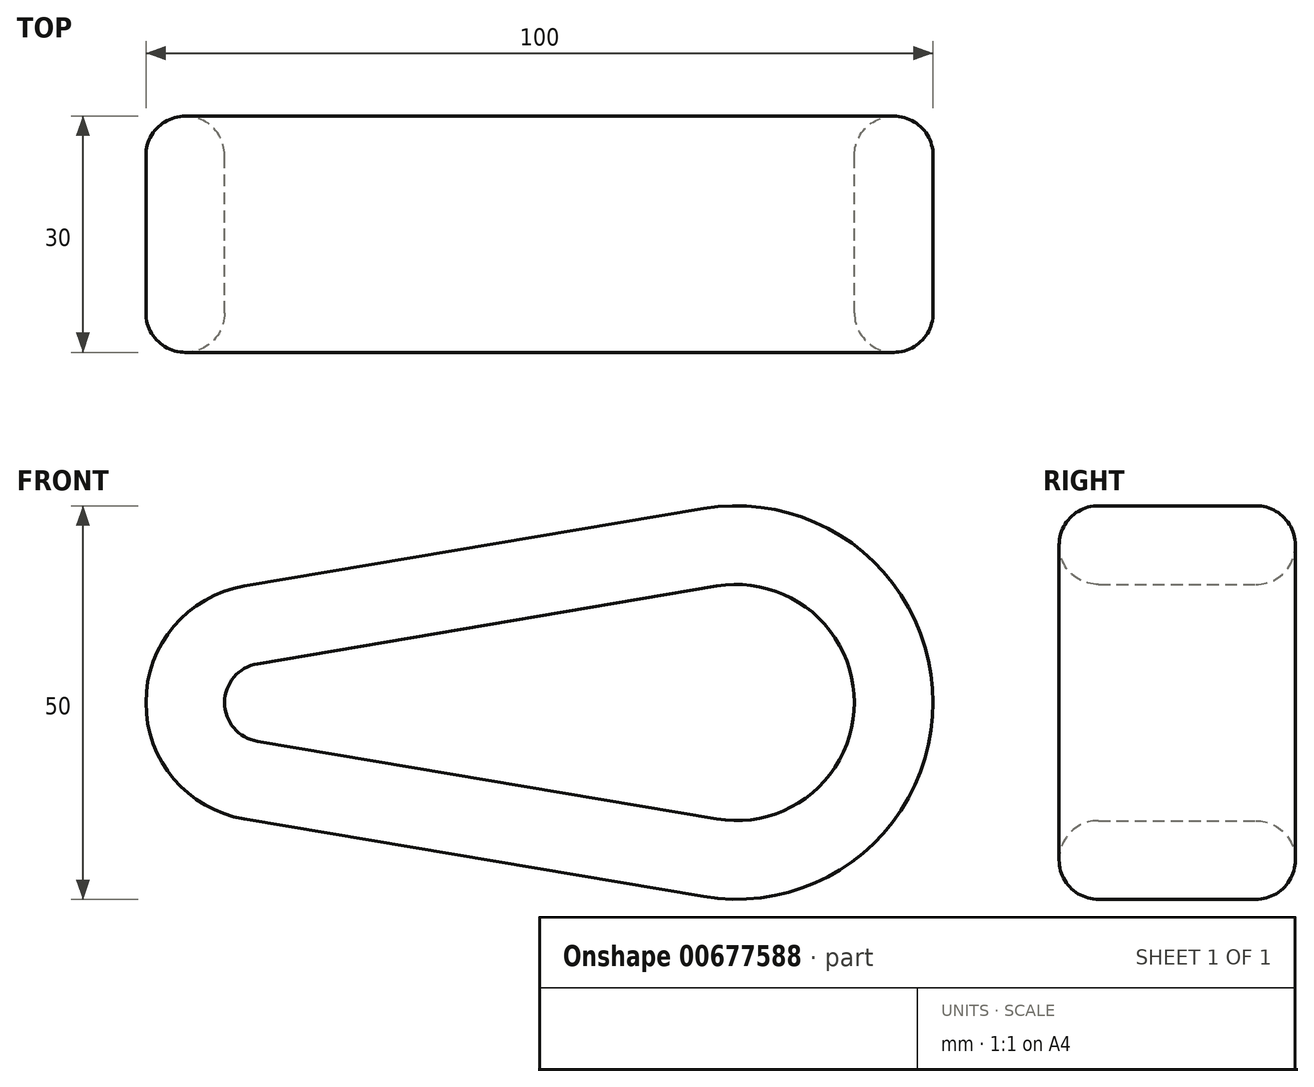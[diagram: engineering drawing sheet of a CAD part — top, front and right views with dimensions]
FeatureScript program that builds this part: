
annotation { "Feature Type Name" : "Feature", "Feature Type Description" : "" }
export const myFeature = defineFeature(function(context is Context, id is Id, definition is map)
    precondition{}
    {
        {
            var Q0;
            Q0=qCreatedBy(makeId("Front.planeOp"),FACE);
            var sketch = newSketch(context, id + "F0", { "sketchPlane" : qUnion([Q0])});
            skArc(sketch, "E0", {"start": v(55.83, -24.65) * mm, "mid": v(85, 0) * mm, "end": v(55.83, 24.65) * mm});
            skArc(sketch, "E1", {"start": v(-2.5, 14.8) * mm, "mid": v(-15, 0) * mm, "end": v(-2.5, -14.8) * mm});
            skLineSegment(sketch, "E2", {"start": v(-2.8, 14.74) * mm, "end": v(55.83, 24.65) * mm});
            skArc(sketch, "E3.MirrorC", {"start": v(-2.5, -14.8) * mm, "mid": v(-15, 0) * mm, "end": v(-2.5, 14.8) * mm});
            skLineSegment(sketch, "E4.MirrorCS", {"start": v(-2.8, -14.74) * mm, "end": v(55.83, -24.65) * mm});
            skLineSegment(sketch, "E5.0", {"start": v(-1.14, 4.88) * mm, "end": v(57.5, 14.8) * mm});
            skLineSegment(sketch, "E6.0", {"start": v(-1.14, -4.88) * mm, "end": v(57.5, -14.8) * mm});
            skArc(sketch, "E7.0", {"start": v(-0.83, -4.93) * mm, "mid": v(-5, 0) * mm, "end": v(-0.83, 4.93) * mm});
            skArc(sketch, "E8.0", {"start": v(57.5, -14.8) * mm, "mid": v(75, 0) * mm, "end": v(57.5, 14.8) * mm});
            skSolve(sketch);
        }
        {
            var Q0;
            {var subQ0=sQuery(id+"F0.wireOp",EDGE,"E0");Q0=makeQuery(id+"F0.imprint","IMPRINT",FACE,{"disambiguationData":[TD([[makeQuery(id+"F0.imprint","IMPRINT",EDGE,{"derivedFrom":subQ0}),1.0]])]});}
            extrude(context, id + "F1", {"entities" : qUnion([Q0]), "depth" : 15 * mm, "offsetDistance" : 25 * mm, "hasSecondDirection" : true, "secondDirectionOppositeDirection" : true, "secondDirectionDepth" : 15 * mm});
        }
        {
            var Q0;
            Q0=makeQuery(id+"F1.opExtrude","CAP_EDGE",EDGE,{"disambiguationData":[OSD([sQuery(id+"F0.wireOp",EDGE,"E5.0")])],"isStart":false});
            var Q1;
            Q1=makeQuery(id+"F1.opExtrude","CAP_EDGE",EDGE,{"disambiguationData":[OSD([sQuery(id+"F0.wireOp",EDGE,"E2")])],"isStart":false});
            var Q2;
            Q2=makeQuery(id+"F1.opExtrude","CAP_EDGE",EDGE,{"disambiguationData":[OSD([sQuery(id+"F0.wireOp",EDGE,"E2")])],"isStart":true});
            var Q3;
            Q3=makeQuery(id+"F1.opExtrude","CAP_EDGE",EDGE,{"disambiguationData":[OSD([sQuery(id+"F0.wireOp",EDGE,"E5.0")])],"isStart":true});
            fillet(context, id + "F2", {"entities" : qUnion([Q0, Q1, Q2, Q3]), "radius" : 5 * mm, "tangentPropagation" : true, "allowEdgeOverflow" : false});
        }
    });
